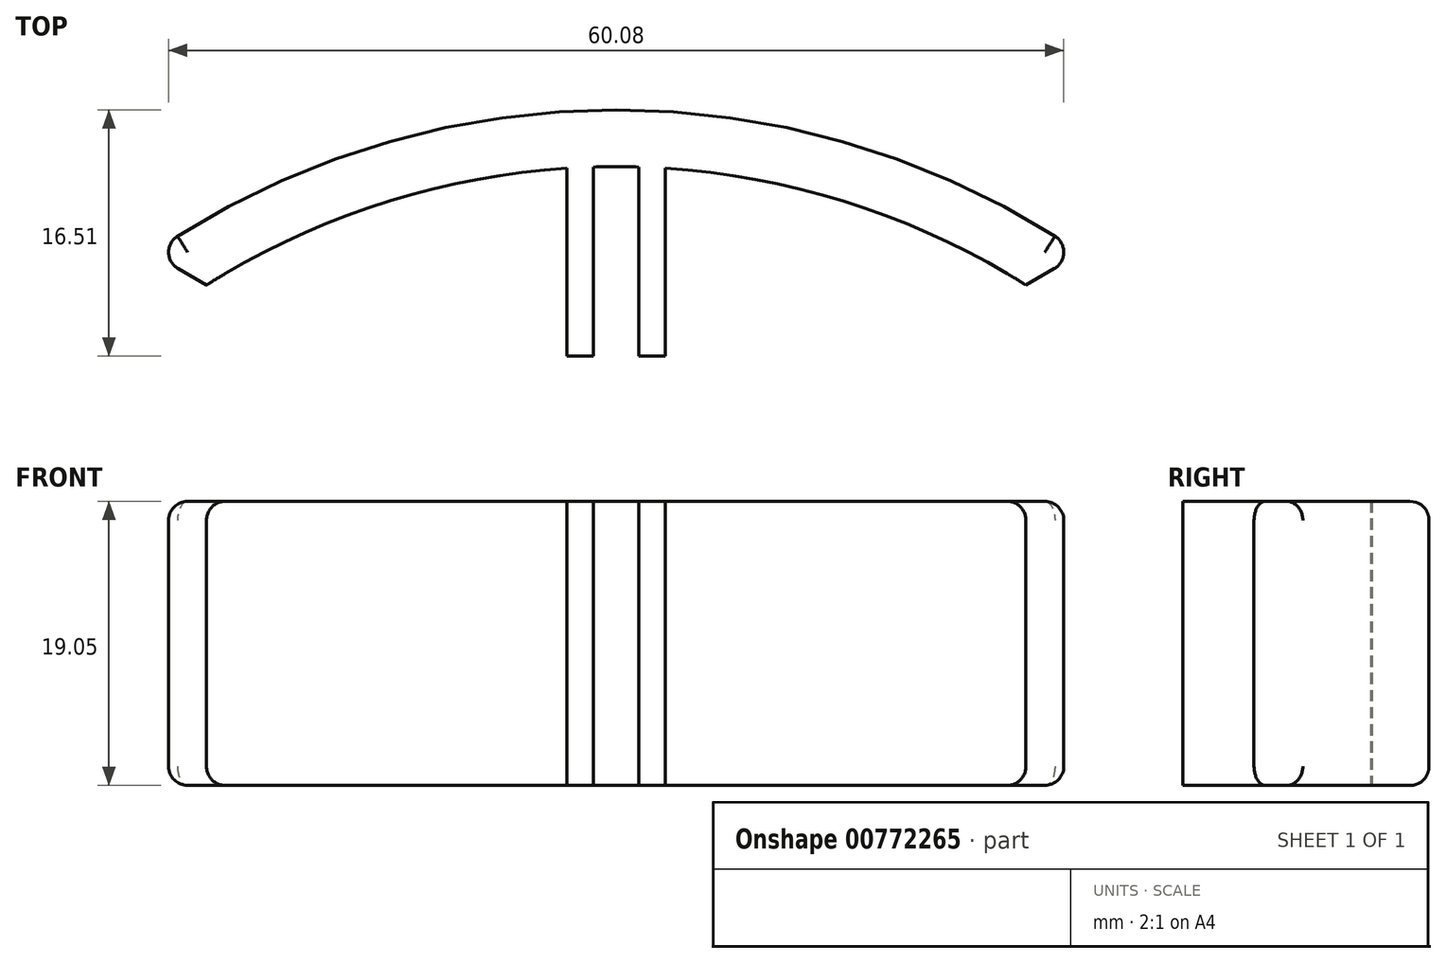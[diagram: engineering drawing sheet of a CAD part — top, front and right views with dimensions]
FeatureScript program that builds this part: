
annotation { "Feature Type Name" : "Feature", "Feature Type Description" : "" }
export const myFeature = defineFeature(function(context is Context, id is Id, definition is map)
    precondition{}
    {
        {
            var Q0;
            Q0=qCreatedBy(makeId("Top.planeOp"),FACE);
            var sketch = newSketch(context, id + "F0", { "sketchPlane" : qUnion([Q0])});
            skPoint(sketch, "E0", {"position": v(0, 23.81) * mm});
            skArc(sketch, "E1", {"start": v(0, 23.81) * mm, "mid": v(-14.3, 21.79) * mm, "end": v(-27.5, 15.88) * mm});
            skArc(sketch, "E2.MirrorCS", {"start": v(0, 23.81) * mm, "mid": v(14.3, 21.79) * mm, "end": v(27.5, 15.88) * mm});
            skArc(sketch, "E3.0", {"start": v(0, 27.62) * mm, "mid": v(-16.32, 25.16) * mm, "end": v(-31.2, 18) * mm});
            skArc(sketch, "E4.MirrorCS", {"start": v(0, 27.62) * mm, "mid": v(16.32, 25.16) * mm, "end": v(31.2, 18) * mm});
            skLineSegment(sketch, "E5", {"start": v(-25.05, 23.81) * mm, "end": v(30.35, 23.81) * mm, "construction": true});
            skLineSegment(sketch, "E6.bottom", {"start": v(-3.3, 23.81) * mm, "end": v(-1.52, 23.81) * mm});
            skLineSegment(sketch, "E6.top", {"start": v(-3.3, 11.11) * mm, "end": v(-1.52, 11.11) * mm});
            skLineSegment(sketch, "E6.left", {"start": v(-3.3, 23.81) * mm, "end": v(-3.3, 11.11) * mm});
            skLineSegment(sketch, "E6.right", {"start": v(-1.52, 23.81) * mm, "end": v(-1.52, 11.11) * mm});
            skLineSegment(sketch, "E7.MirrorCS", {"start": v(1.52, 23.81) * mm, "end": v(1.52, 11.11) * mm});
            skLineSegment(sketch, "E8.MirrorCS", {"start": v(3.3, 11.11) * mm, "end": v(1.52, 11.11) * mm});
            skLineSegment(sketch, "E9.MirrorCS", {"start": v(3.3, 23.81) * mm, "end": v(3.3, 11.11) * mm});
            skLineSegment(sketch, "E10", {"start": v(0, 0) * mm, "end": v(-27.5, 15.88) * mm, "construction": true});
            skLineSegment(sketch, "E11", {"start": v(-27.5, 15.88) * mm, "end": v(-31.2, 18) * mm});
            skLineSegment(sketch, "E12.MirrorCS", {"start": v(27.5, 15.88) * mm, "end": v(31.2, 18) * mm});
            skSolve(sketch);
        }
        {
            var Q0;
            Q0=qSketchRegion(id+"F0",true);
            extrude(context, id + "F1", {"entities" : qUnion([Q0]), "depth" : 19.05 * mm, "offsetDistance" : 25.4 * mm});
        }
        {
            var Q0;
            Q0=makeQuery(id+"F1.opExtrude","CAP_EDGE",EDGE,{"disambiguationData":[OSD([sQuery(id+"F0.wireOp",EDGE,"E3.0"),sQuery(id+"F0.wireOp",EDGE,"E4.MirrorCS")])],"isStart":false});
            var Q1;
            Q1=makeQuery(id+"F1.opExtrude","CAP_EDGE",EDGE,{"disambiguationData":[OSD([sQuery(id+"F0.wireOp",EDGE,"E3.0"),sQuery(id+"F0.wireOp",EDGE,"E4.MirrorCS")])],"isStart":true});
            fillet(context, id + "F2", {"entities" : qUnion([Q0, Q1]), "radius" : 1.27 * mm, "tangentPropagation" : true, "allowEdgeOverflow" : false});
        }
        {
            var Q0;
            Q0=makeQuery(id+"F1.opExtrude","SWEPT_EDGE",EDGE,{"disambiguationData":[OSD([sQuery(id+"F0.wireOp",EDGE,"E3.0"),sQuery(id+"F0.wireOp",EDGE,"E11")])]});
            var Q1;
            Q1=makeQuery(id+"F1.opExtrude","SWEPT_EDGE",EDGE,{"disambiguationData":[OSD([sQuery(id+"F0.wireOp",EDGE,"E4.MirrorCS"),sQuery(id+"F0.wireOp",EDGE,"E12.MirrorCS")])]});
            fillet(context, id + "F3", {"entities" : qUnion([Q0, Q1]), "radius" : 1.27 * mm, "tangentPropagation" : true, "allowEdgeOverflow" : false});
        }
    });
